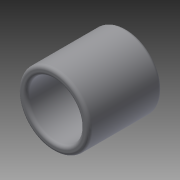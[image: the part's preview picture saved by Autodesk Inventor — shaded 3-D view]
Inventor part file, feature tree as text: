
AUTODESK INVENTOR PART (.ipt)
format: ipt  version: 2014 (Build 180170000, 170)  size: 129,024 bytes
history: native  units: in
note: dims shown in document units (in); Inventor stores cm internally (conversion verified against a paired STEP export)
features: extrude x1, fillet x1, sketch x1
ambient origin geometry x8: Origin, YZ Plane, XZ Plane, XY Plane, X Axis, Y Axis, Z Axis, Center Point
bodies: Solid1 (feature_tree)
feature tree (3):
  extrude  "Extrusion1"  Depth=0.025in
  fillet  "Fillet1"  Radius=0.54in
  sketch  "Sketch1"  dims[d0=0.525in d1=0.4in d2=0.54in d3=0.0in d4=0.025in]
